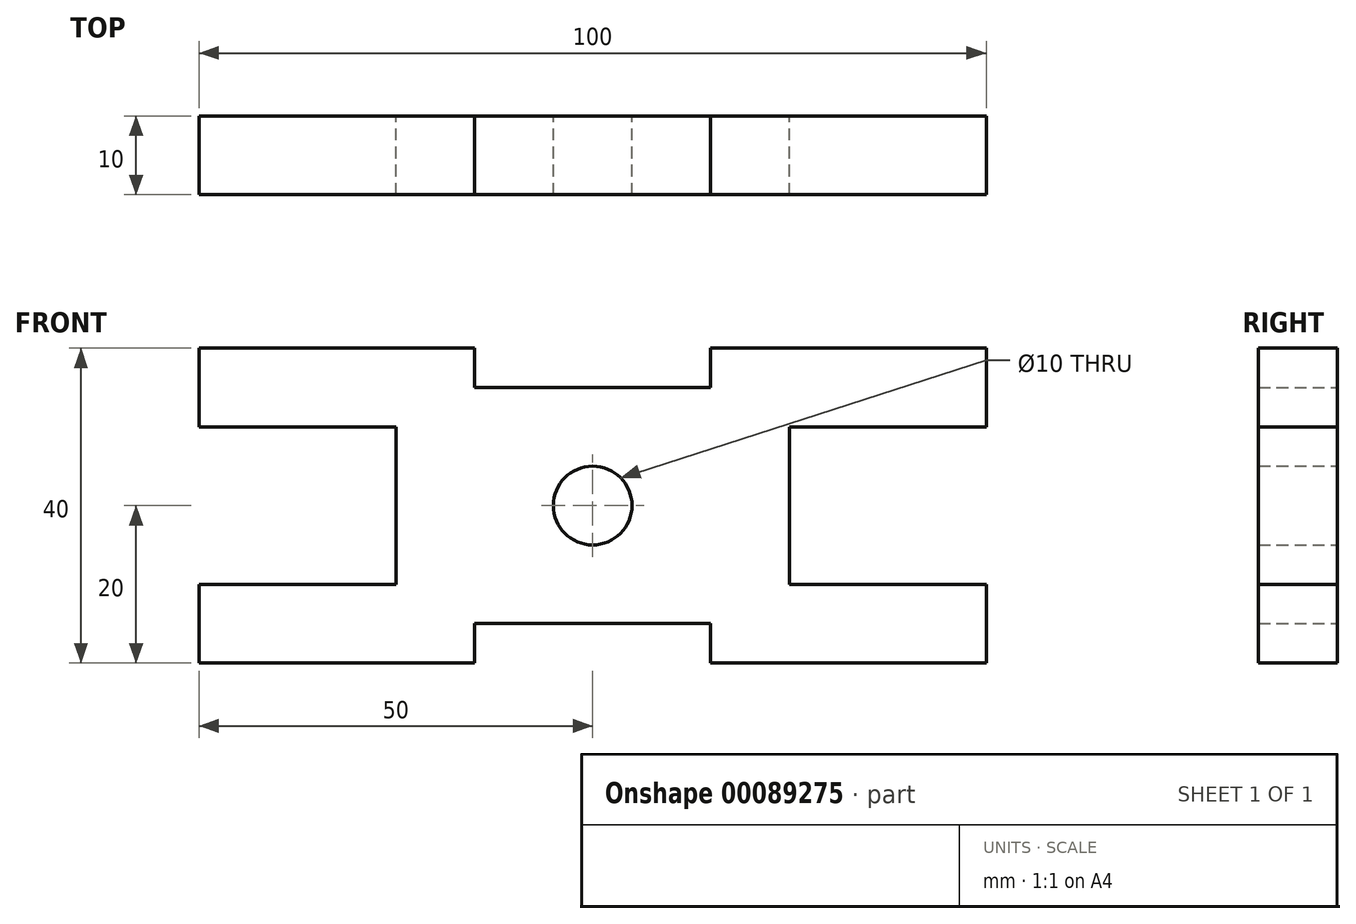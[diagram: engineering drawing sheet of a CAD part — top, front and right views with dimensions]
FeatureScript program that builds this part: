
annotation { "Feature Type Name" : "Feature", "Feature Type Description" : "" }
export const myFeature = defineFeature(function(context is Context, id is Id, definition is map)
    precondition{}
    {
        {
            var Q0;
            Q0=qCreatedBy(makeId("Front.planeOp"),FACE);
            var sketch = newSketch(context, id + "F0", { "sketchPlane" : qUnion([Q0])});
            skArc(sketch, "E0", {"start": v(0, 5) * mm, "mid": v(3.54, 3.54) * mm, "end": v(5, 0) * mm});
            skLineSegment(sketch, "E1", {"start": v(5, 0) * mm, "end": v(25, 0) * mm, "construction": true});
            skLineSegment(sketch, "E2", {"start": v(25, 0) * mm, "end": v(25, 10) * mm});
            skLineSegment(sketch, "E3", {"start": v(25, 10) * mm, "end": v(50, 10) * mm});
            skLineSegment(sketch, "E4", {"start": v(50, 10) * mm, "end": v(50, 20) * mm});
            skLineSegment(sketch, "E5", {"start": v(50, 20) * mm, "end": v(15, 20) * mm});
            skLineSegment(sketch, "E6", {"start": v(15, 20) * mm, "end": v(15, 15) * mm});
            skLineSegment(sketch, "E7", {"start": v(15, 15) * mm, "end": v(0, 15) * mm});
            skLineSegment(sketch, "E8", {"start": v(0, 15) * mm, "end": v(0, 5) * mm, "construction": true});
            skArc(sketch, "E9.MirrorCS", {"start": v(0, 5) * mm, "mid": v(-3.54, 3.54) * mm, "end": v(-5, 0) * mm});
            skLineSegment(sketch, "E10.MirrorCS", {"start": v(-25, 0) * mm, "end": v(-25, 10) * mm});
            skLineSegment(sketch, "E11.MirrorCS", {"start": v(-5, 0) * mm, "end": v(-25, 0) * mm, "construction": true});
            skLineSegment(sketch, "E12.MirrorCS", {"start": v(-15, 20) * mm, "end": v(-15, 15) * mm});
            skLineSegment(sketch, "E13.MirrorCS", {"start": v(-25, 10) * mm, "end": v(-50, 10) * mm});
            skLineSegment(sketch, "E14.MirrorCS", {"start": v(-15, 15) * mm, "end": v(0, 15) * mm});
            skLineSegment(sketch, "E15.MirrorCS", {"start": v(-50, 20) * mm, "end": v(-15, 20) * mm});
            skLineSegment(sketch, "E16.MirrorCS", {"start": v(-50, 10) * mm, "end": v(-50, 20) * mm});
            skLineSegment(sketch, "E17.MirrorCS", {"start": v(-25, 0) * mm, "end": v(-25, -10) * mm});
            skLineSegment(sketch, "E18.MirrorCS", {"start": v(25, -10) * mm, "end": v(50, -10) * mm});
            skArc(sketch, "E19.MirrorCS", {"start": v(0, -5) * mm, "mid": v(-3.54, -3.54) * mm, "end": v(-5, 0) * mm});
            skLineSegment(sketch, "E20.MirrorCS", {"start": v(15, -15) * mm, "end": v(0, -15) * mm});
            skLineSegment(sketch, "E21.MirrorCS", {"start": v(25, 0) * mm, "end": v(25, -10) * mm});
            skLineSegment(sketch, "E22.MirrorCS", {"start": v(-25, -10) * mm, "end": v(-50, -10) * mm});
            skLineSegment(sketch, "E23.MirrorCS", {"start": v(-15, -15) * mm, "end": v(0, -15) * mm});
            skLineSegment(sketch, "E24.MirrorCS", {"start": v(15, -20) * mm, "end": v(15, -15) * mm});
            skLineSegment(sketch, "E25.MirrorCS", {"start": v(-50, -20) * mm, "end": v(-15, -20) * mm});
            skLineSegment(sketch, "E26.MirrorCS", {"start": v(50, -10) * mm, "end": v(50, -20) * mm});
            skArc(sketch, "E27.MirrorCS", {"start": v(0, -5) * mm, "mid": v(3.54, -3.54) * mm, "end": v(5, 0) * mm});
            skLineSegment(sketch, "E28.MirrorCS", {"start": v(0, -15) * mm, "end": v(0, -5) * mm, "construction": true});
            skLineSegment(sketch, "E29.MirrorCS", {"start": v(50, -20) * mm, "end": v(15, -20) * mm});
            skLineSegment(sketch, "E30.MirrorCS", {"start": v(-50, -10) * mm, "end": v(-50, -20) * mm});
            skLineSegment(sketch, "E31.MirrorCS", {"start": v(-15, -20) * mm, "end": v(-15, -15) * mm});
            skSolve(sketch);
        }
        {
            var Q0;
            Q0 = qSketchRegion(id + "F0", true);
            extrude(context, id + "F1", {"entities" : qUnion([Q0]), "depth" : 10 * mm});
        }
    });
